# Revit family: Furniture_Other_Sjobergs_Workbench_750
name_source: partatom
category: Furniture
revit_build: Autodesk Revit 2017 (Build: 20190508_0315(x64)
units: mm (PartAtom-declared; Revit-internal decimal feet)

## family parameters
Always vertical = Yes
Cut with Voids When Loaded = No
OmniClass Number = 23.40.70.14
OmniClass Title = Retail and Commercial Equipment and Furnishings
Room Calculation Point = No
Shared = No
Work Plane-Based = No

## types (1)
- 33074 Sjoberg Complete Working Height 750 mm
    AssetType = Movable
    BIMObjectName = Furniture_Other_Sjobergs_Workbench_750
    Brand = Sjöbergs
    Category = School, Woodwork
    Collection = Planer Benches
    Color = Wooden
    Constituents = 33110 Bench top + 33160 Front vise + 33231 Wooden trestle + 33383 Jaw cushions front vise + 33384 Jaw cushions shoulder vise + 33636 Holdfast with insert
    ConvergoRefNr = 0184-2005-0004-SE
    Cost = 0 $
    Description = The top is constructed in solid, lacquered beech. The area of the top surface is 1070x405 mm and the thickness is 60 mm. Bench dogs are included. The vice sliding mechanism is smooth and if necessary can be easily adjusted. An optimal Sjobergs Front Vice 33160 can be fitted to each workbench which would increase the working possibilities.
    DurationUnit = Year
    Features = Traditional designed and sturdily built.
    Finish = Bench top and trestle in lacquered beech.
    IfcExportAs = IfcFurnishingElementType
    IfcExportType = TABLE
    MainColor = Wooden
    Manufacturer = Sjöbergs
    ManufacturerName = Sjöbergs
    ManufacturerURL = https://www.sjobergs.se
    Material = Wood
    Model = 33074 Sjoberg Complete Working Height 750 mm
    ModelReference = 33074
    NBSDescription = School art, design and technology tables and workbenches;
    NBSReference = 45-35-20/320
    Name = Sjobergs_Workbench_750
    NominalDepth = 405 mm
    NominalLength = 1270 mm
    ProductDatasheet = https://www.sjobergs.se
    ProductInformation = The top is constructed in solid, lacquered beech. The area of the top surface is 1070x405 mm and the thickness is 60 mm. Bench dogs are included. The vice sliding mechanism is smooth and if necessary can be easily adjusted. An optimal Sjobergs Front Vice 33160 can be fitted to each workbench which would increase the working possibilities.
    Shape = Sculptured
    Size = 1270x405x750 mm
    TableMainMaterial = Beech
    TableSecondaryMaterial = Ash
    URL = https://www.sjobergs.se
    Uniclass2 = Pr_40_50_21
    Uniclass2015Description = Desks, Tables And Worktops
    Uniclass2015Reference = Pr_40_50_21_76
    Version = 1
    VersionDate = 26/06/2020
    WarrantyDurationUnit = Year
    Weight = 21 kg + 11 kg

## geometry (parser evidence)
native form markers: Sweep x6
no freeform markers — native parametric forms only
